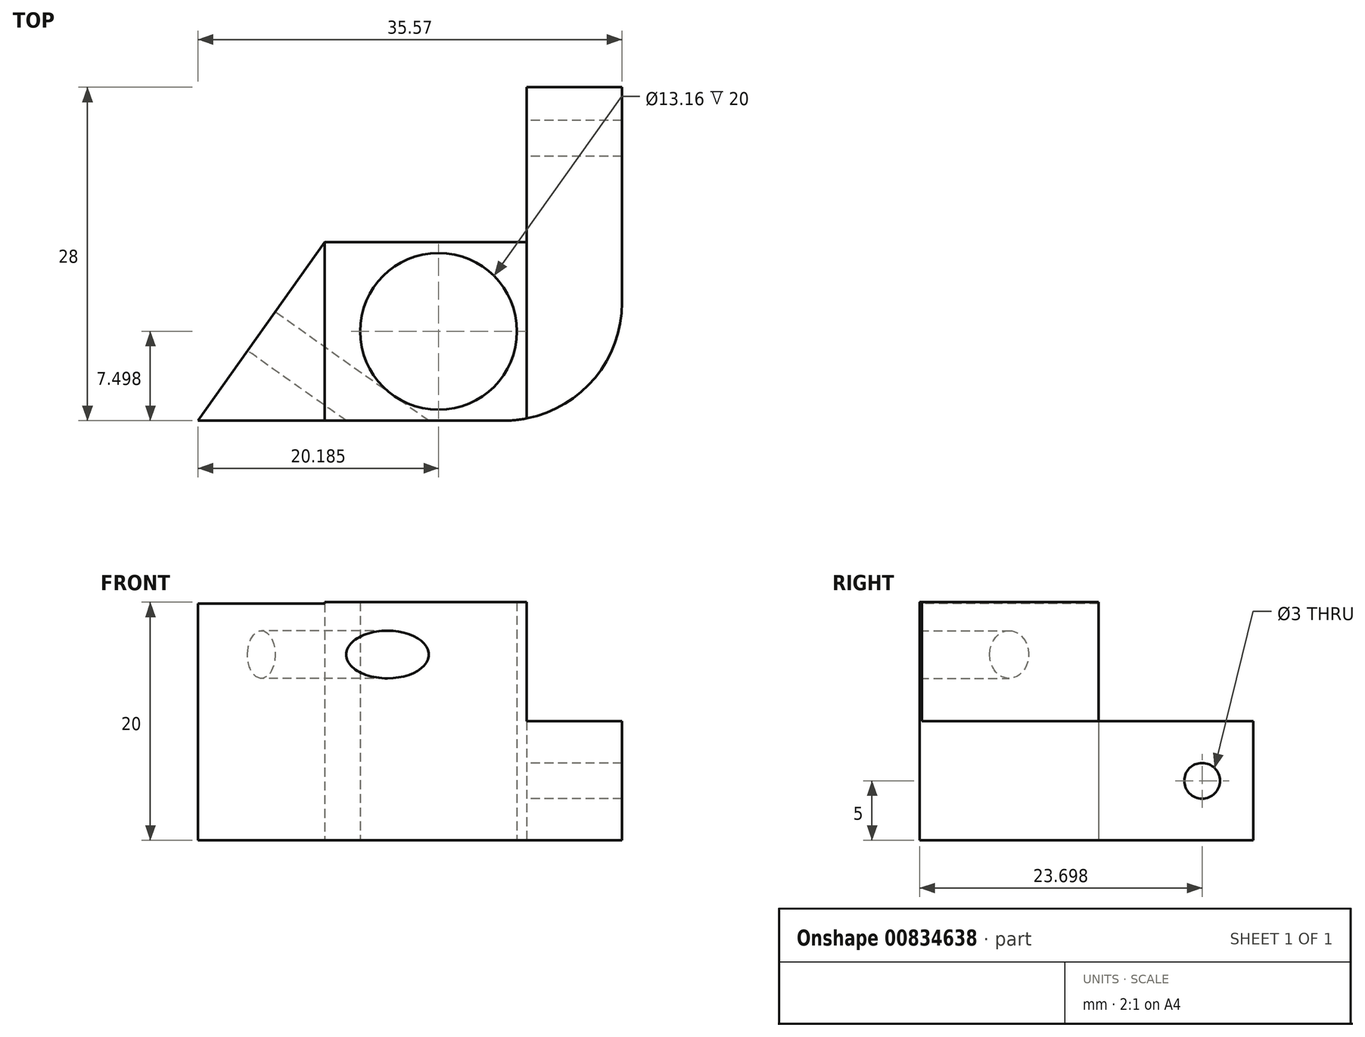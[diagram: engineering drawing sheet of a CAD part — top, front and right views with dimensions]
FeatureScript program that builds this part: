
annotation { "Feature Type Name" : "Feature", "Feature Type Description" : "" }
export const myFeature = defineFeature(function(context is Context, id is Id, definition is map)
    precondition{}
    {
        {
            var Q0;
            Q0=qCreatedBy(makeId("Top.planeOp"),FACE);
            var sketch = newSketch(context, id + "F0", { "sketchPlane" : qUnion([Q0])});
            skLineSegment(sketch, "E0.bottom", {"start": v(-7.29, 15.05) * mm, "end": v(0.71, 15.05) * mm});
            skLineSegment(sketch, "E0.top", {"start": v(-7.29, 2.05) * mm, "end": v(0.71, 2.05) * mm});
            skLineSegment(sketch, "E0.left", {"start": v(-7.29, 15.05) * mm, "end": v(-7.29, 2.05) * mm});
            skLineSegment(sketch, "E0.right", {"start": v(0.71, 15.05) * mm, "end": v(0.71, 2.05) * mm});
            skLineSegment(sketch, "E1.bottom", {"start": v(0.71, 2.05) * mm, "end": v(-24.24, 2.05) * mm});
            skLineSegment(sketch, "E1.top", {"start": v(0.71, -12.95) * mm, "end": v(-24.24, -12.95) * mm});
            skLineSegment(sketch, "E1.left", {"start": v(0.71, 2.05) * mm, "end": v(0.71, -12.95) * mm});
            skLineSegment(sketch, "E1.right", {"start": v(-24.24, 2.05) * mm, "end": v(-24.24, -12.95) * mm});
            skLineSegment(sketch, "E2", {"start": v(-24.24, -5.45) * mm, "end": v(0.71, -5.45) * mm});
            skCircle(sketch, "E3", {"center": v(-14.67, -5.45) * mm, "radius": 6.58 * mm});
            skLineSegment(sketch, "E4", {"start": v(-24.24, -12.95) * mm, "end": v(-34.86, -12.95) * mm});
            skLineSegment(sketch, "E5", {"start": v(-34.86, -12.95) * mm, "end": v(-24.24, 2.05) * mm});
            skSolve(sketch);
        }
        {
            var Q0;
            Q0=makeQuery(id+"F0.imprint","IMPRINT",FACE,{"disambiguationData":[TD([[makeQuery(id+"F0.imprint","IMPRINT",EDGE,{"derivedFrom":sQuery(id+"F0.wireOp",EDGE,"E0.bottom")}),-1.0]])]});
            var Q1;
            {var subQ1=sQuery(id+"F0.wireOp",EDGE,"E1.bottom");var subQ5=makeQuery(id+"F0.imprint","INTERSECT",VERTEX,{"derivedFrom":[sQuery(id+"F0.wireOp",EDGE,"E0.left"),subQ1]});Q1=makeQuery(id+"F0.imprint","IMPRINT",FACE,{"disambiguationData":[TD([[makeQuery(id+"F0.imprint","IMPRINT",EDGE,{"disambiguationData":[TD([[subQ5,-1.0]])],"derivedFrom":subQ1}),1.0]])]});}
            var Q2;
            {var subQ1=sQuery(id+"F0.wireOp",EDGE,"E1.top");Q2=makeQuery(id+"F0.imprint","IMPRINT",FACE,{"disambiguationData":[TD([[makeQuery(id+"F0.imprint","IMPRINT",EDGE,{"derivedFrom":subQ1}),-1.0]])]});}
            extrude(context, id + "F1", {"entities" : qUnion([Q0, Q1, Q2]), "depth" : 10 * mm, "offsetDistance" : 25 * mm});
        }
        {
            var Q0;
            Q0=makeQuery(id+"F1.opExtrude","SWEPT_EDGE",EDGE,{"disambiguationData":[OSD([sQuery(id+"F0.wireOp",EDGE,"E1.top"),sQuery(id+"F0.wireOp",EDGE,"E1.left")])]});
            fillet(context, id + "F2", {"entities" : qUnion([Q0]), "radius" : 9.9 * mm, "tangentPropagation" : true, "allowEdgeOverflow" : false});
        }
        {
            var Q0;
            Q0=makeQuery(id+"F1.opExtrude","SWEPT_FACE",FACE,{"disambiguationData":[OSD([sQuery(id+"F0.wireOp",EDGE,"E0.left")])]});
            var sketch = newSketch(context, id + "F3", { "sketchPlane" : qUnion([Q0])});
            skCircle(sketch, "E6", {"center": v(-10.75, 5) * mm, "radius": 2 * mm});
            skPoint(sketch, "E7", {"position": v(-15.05, 5) * mm});
            skSolve(sketch);
        }
        {
            var Q0;
            Q0=sQuery(id+"F3.wireOp",VERTEX,"E6.center");
            var Q1;
            Q1=makeQuery(id+"F1.opExtrude","SWEPT_BODY",BODY,{"disambiguationData":[OSD([sQuery(id+"F0.wireOp",EDGE,"E0.bottom"),sQuery(id+"F0.wireOp",EDGE,"E0.left"),sQuery(id+"F0.wireOp",EDGE,"E0.right"),sQuery(id+"F0.wireOp",EDGE,"E1.bottom"),sQuery(id+"F0.wireOp",EDGE,"E1.top"),sQuery(id+"F0.wireOp",EDGE,"E1.left"),sQuery(id+"F0.wireOp",EDGE,"E1.right"),sQuery(id+"F0.wireOp",EDGE,"KIV5i79b-hAaV-w3dH-wgyL-2EISkAxxYOQ8")])]});
            hole(context, id + "F4", {"style" : HoleStyle.SIMPLE, "endStyle" : HoleEndStyle.THROUGH, "holeDiameter" : 3 * mm, "majorDiameter" : 4 * mm, "isTappedThrough" : true, "tappedDepth" : 12 * mm, "tapClearance" : 3, "locations" : qUnion([Q0]), "scope" : qUnion([Q1])});
        }
        {
            var Q0;
            Q0=makeQuery(id+"F1.opExtrude","CAP_FACE",FACE,{"disambiguationData":[OSD([sQuery(id+"F0.wireOp",EDGE,"E0.bottom"),sQuery(id+"F0.wireOp",EDGE,"E0.left"),sQuery(id+"F0.wireOp",EDGE,"E0.right"),sQuery(id+"F0.wireOp",EDGE,"E1.bottom"),sQuery(id+"F0.wireOp",EDGE,"E1.top"),sQuery(id+"F0.wireOp",EDGE,"E1.left"),sQuery(id+"F0.wireOp",EDGE,"E1.right"),sQuery(id+"F0.wireOp",EDGE,"E3")])],"isStart":false});
            var sketch = newSketch(context, id + "F5", { "sketchPlane" : qUnion([Q0])});
            skLineSegment(sketch, "E8", {"start": v(-7.29, 2.05) * mm, "end": v(-7.29, -12.77) * mm});
            skSolve(sketch);
        }
        {
            var Q0;
            {var subQ8=sQuery(id+"F5.wireOp",EDGE,"E8");Q0=makeQuery(id+"F5.imprint","IMPRINT",FACE,{"disambiguationData":[TD([[makeQuery(id+"F5.imprint","IMPRINT",EDGE,{"derivedFrom":subQ8}),-1.0]])]});}
            extrude(context, id + "F6", {"entities" : qUnion([Q0]), "operationType" : NewBodyOperationType.ADD, "depth" : 10 * mm, "offsetDistance" : 25 * mm});
        }
        {
            var Q0;
            {var subQ3=sQuery(id+"F0.wireOp",EDGE,"E4");Q0=makeQuery(id+"F0.imprint","IMPRINT",FACE,{"disambiguationData":[TD([[makeQuery(id+"F0.imprint","IMPRINT",EDGE,{"derivedFrom":subQ3}),-1.0]])]});}
            extrude(context, id + "F7", {"entities" : qUnion([Q0]), "operationType" : NewBodyOperationType.ADD, "depth" : 19.9 * mm, "offsetDistance" : 25 * mm});
        }
        {
            var Q0;
            Q0=makeQuery(id+"F7.opExtrude","SWEPT_FACE",FACE,{"disambiguationData":[OSD([sQuery(id+"F0.wireOp",EDGE,"E5")])]});
            var sketch = newSketch(context, id + "F8", { "sketchPlane" : qUnion([Q0])});
            skCircle(sketch, "E9", {"center": v(21.53, 15.6) * mm, "radius": 1.9 * mm});
            skPoint(sketch, "E9.centerSnap0", {"position": v(21.53, 19.9) * mm});
            skSolve(sketch);
        }
        {
            var Q0;
            Q0=sQuery(id+"F8.wireOp",VERTEX,"E9.center");
            var Q1;
            Q1=makeQuery(id+"F1.opExtrude","SWEPT_BODY",BODY,{"disambiguationData":[OSD([sQuery(id+"F0.wireOp",EDGE,"E0.bottom"),sQuery(id+"F0.wireOp",EDGE,"E0.left"),sQuery(id+"F0.wireOp",EDGE,"E0.right"),sQuery(id+"F0.wireOp",EDGE,"E1.bottom"),sQuery(id+"F0.wireOp",EDGE,"E1.top"),sQuery(id+"F0.wireOp",EDGE,"E1.left"),sQuery(id+"F0.wireOp",EDGE,"E1.right"),sQuery(id+"F0.wireOp",EDGE,"E3")])]});
            hole(context, id + "F9", {"style" : HoleStyle.SIMPLE, "endStyle" : HoleEndStyle.THROUGH, "holeDiameter" : 4 * mm, "majorDiameter" : 5 * mm, "isTappedThrough" : true, "tappedDepth" : 12 * mm, "tapClearance" : 3, "locations" : qUnion([Q0]), "scope" : qUnion([Q1])});
        }
    });
